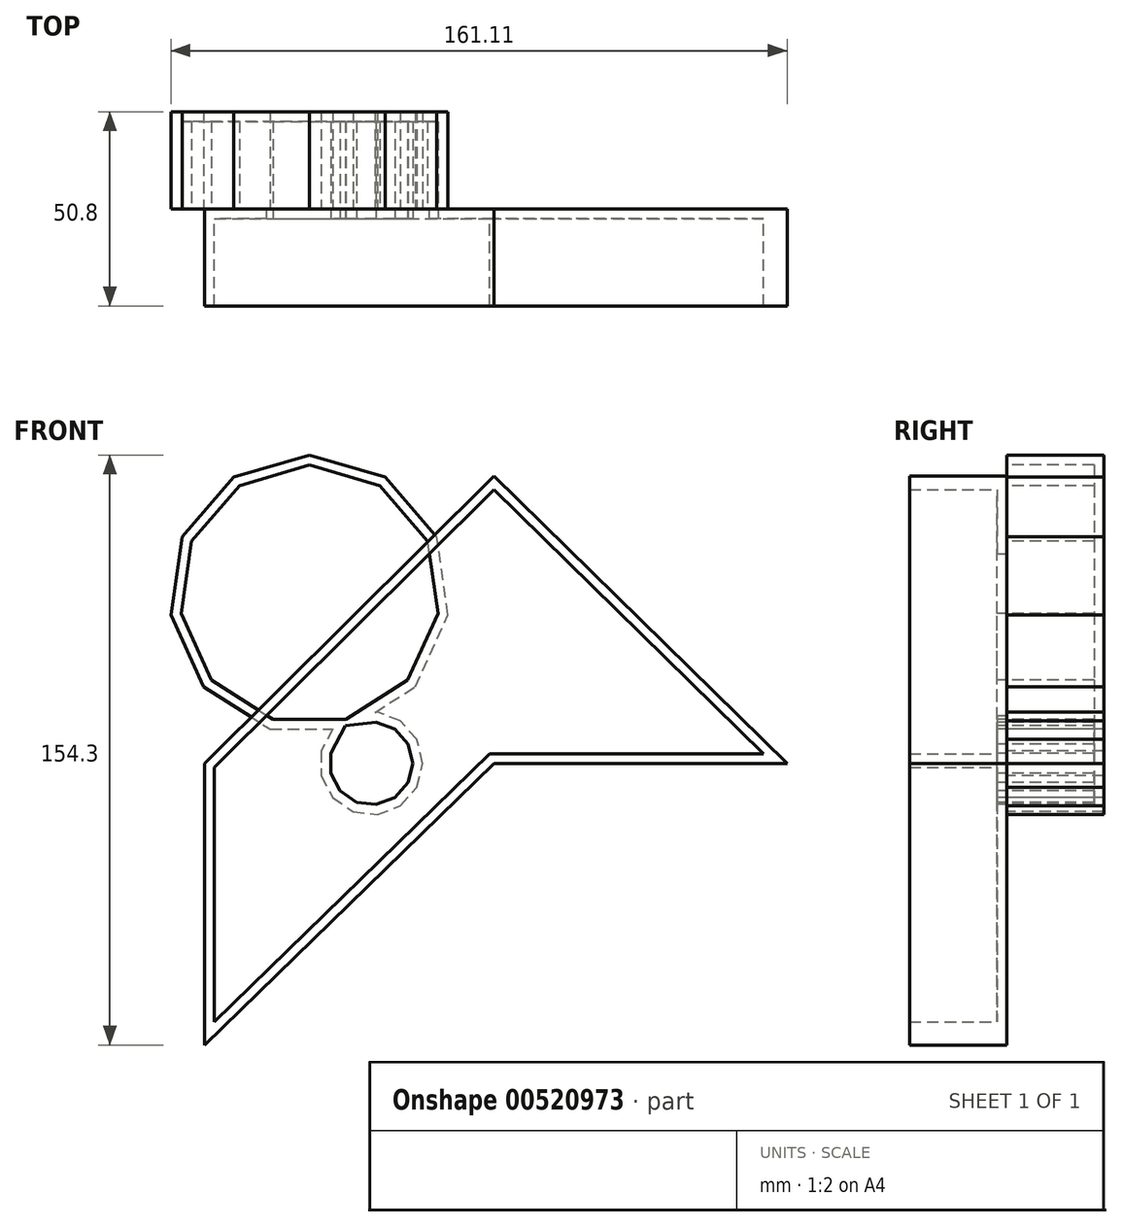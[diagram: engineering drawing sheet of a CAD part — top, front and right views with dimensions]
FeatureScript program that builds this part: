
annotation { "Feature Type Name" : "Feature", "Feature Type Description" : "" }
export const myFeature = defineFeature(function(context is Context, id is Id, definition is map)
    precondition{}
    {
        {
            var Q0;
            Q0=qCreatedBy(makeId("Front.planeOp"),FACE);
            var sketch = newSketch(context, id + "F0", { "sketchPlane" : qUnion([Q0])});
            skLineSegment(sketch, "E0", {"start": v(0, 75.14) * mm, "end": v(-75.6, 0) * mm});
            skLineSegment(sketch, "E1", {"start": v(-75.6, 0) * mm, "end": v(-75.6, -73.66) * mm});
            skLineSegment(sketch, "E2", {"start": v(-75.6, -73.66) * mm, "end": v(0, 0) * mm});
            skLineSegment(sketch, "E3", {"start": v(0, 0) * mm, "end": v(76.7, 0) * mm});
            skLineSegment(sketch, "E4", {"start": v(76.7, 0) * mm, "end": v(0, 75.14) * mm});
            skSolve(sketch);
        }
        {
            var Q0;
            Q0=makeQuery(id+"F0.imprint","IMPRINT",FACE,{"disambiguationData":[TD([[makeQuery(id+"F0.imprint","IMPRINT",EDGE,{"derivedFrom":sQuery(id+"F0.wireOp",EDGE,"E0")}),1.0]])]});
            extrude(context, id + "F1", {"entities" : qUnion([Q0]), "depth" : 25.4 * mm, "offsetDistance" : 25.4 * mm});
        }
        {
            var Q0;
            Q0=makeQuery(id+"F1.opExtrude","CAP_FACE",FACE,{"disambiguationData":[OSD([sQuery(id+"F0.wireOp",EDGE,"E0"),sQuery(id+"F0.wireOp",EDGE,"E1"),sQuery(id+"F0.wireOp",EDGE,"E2"),sQuery(id+"F0.wireOp",EDGE,"E3"),sQuery(id+"F0.wireOp",EDGE,"E4")])],"isStart":false});
            shell(context, id + "F2", {"entities" : qUnion([Q0]), "thickness" : 2.54 * mm});
        }
        {
            var Q0;
            Q0=makeQuery(id+"F1.opExtrude","CAP_FACE",FACE,{"disambiguationData":[OSD([sQuery(id+"F0.wireOp",EDGE,"E0"),sQuery(id+"F0.wireOp",EDGE,"E1"),sQuery(id+"F0.wireOp",EDGE,"E2"),sQuery(id+"F0.wireOp",EDGE,"E3"),sQuery(id+"F0.wireOp",EDGE,"E4")])],"isStart":true});
            var sketch = newSketch(context, id + "F3", { "sketchPlane" : qUnion([Q0])});
            skCircle(sketch, "E5.cCircle", {"center": v(32.06, 0) * mm, "radius": 13.08 * mm, "construction": true});
            skLineSegment(sketch, "E5.0", {"start": v(45.14, 3.22) * mm, "end": v(45.14, -3.22) * mm});
            skLineSegment(sketch, "E5.1", {"start": v(45.14, -3.22) * mm, "end": v(42.15, -8.93) * mm});
            skLineSegment(sketch, "E5.2", {"start": v(42.15, -8.93) * mm, "end": v(36.84, -12.6) * mm});
            skLineSegment(sketch, "E5.3", {"start": v(36.84, -12.6) * mm, "end": v(30.44, -13.37) * mm});
            skLineSegment(sketch, "E5.4", {"start": v(30.44, -13.37) * mm, "end": v(24.41, -11.09) * mm});
            skLineSegment(sketch, "E5.5", {"start": v(24.41, -11.09) * mm, "end": v(20.14, -6.26) * mm});
            skLineSegment(sketch, "E5.6", {"start": v(20.14, -6.26) * mm, "end": v(18.6, 0) * mm});
            skLineSegment(sketch, "E5.7", {"start": v(18.6, 0) * mm, "end": v(20.14, 6.26) * mm});
            skLineSegment(sketch, "E5.8", {"start": v(20.14, 6.26) * mm, "end": v(24.41, 11.09) * mm});
            skLineSegment(sketch, "E5.9", {"start": v(24.41, 11.09) * mm, "end": v(30.44, 13.37) * mm});
            skLineSegment(sketch, "E5.10", {"start": v(30.44, 13.37) * mm, "end": v(36.84, 12.6) * mm});
            skLineSegment(sketch, "E5.11", {"start": v(36.84, 12.6) * mm, "end": v(42.15, 8.93) * mm});
            skLineSegment(sketch, "E5.12", {"start": v(42.15, 8.93) * mm, "end": v(45.14, 3.22) * mm});
            skPoint(sketch, "E5.0.midPoint", {"position": v(45.14, 0) * mm});
            skCircle(sketch, "E6.cCircle", {"center": v(48.19, 44.05) * mm, "radius": 35.11 * mm, "construction": true});
            skLineSegment(sketch, "E6.0", {"start": v(58.5, 8.93) * mm, "end": v(37.88, 8.93) * mm});
            skLineSegment(sketch, "E6.1", {"start": v(37.88, 8.93) * mm, "end": v(20.53, 20.08) * mm});
            skLineSegment(sketch, "E6.2", {"start": v(20.53, 20.08) * mm, "end": v(11.97, 38.84) * mm});
            skLineSegment(sketch, "E6.3", {"start": v(11.97, 38.84) * mm, "end": v(14.9, 59.25) * mm});
            skLineSegment(sketch, "E6.4", {"start": v(14.9, 59.25) * mm, "end": v(28.4, 74.83) * mm});
            skLineSegment(sketch, "E6.5", {"start": v(28.4, 74.83) * mm, "end": v(48.19, 80.64) * mm});
            skLineSegment(sketch, "E6.6", {"start": v(48.19, 80.64) * mm, "end": v(67.97, 74.83) * mm});
            skLineSegment(sketch, "E6.7", {"start": v(67.97, 74.83) * mm, "end": v(81.48, 59.25) * mm});
            skLineSegment(sketch, "E6.8", {"start": v(81.48, 59.25) * mm, "end": v(84.41, 38.84) * mm});
            skLineSegment(sketch, "E6.9", {"start": v(84.41, 38.84) * mm, "end": v(75.85, 20.08) * mm});
            skLineSegment(sketch, "E6.10", {"start": v(75.85, 20.08) * mm, "end": v(58.5, 8.93) * mm});
            skPoint(sketch, "E6.0.midPoint", {"position": v(48.19, 8.93) * mm});
            skSolve(sketch);
        }
        {
            var Q0;
            Q0 = qSketchRegion(id + "F3", true);
            extrude(context, id + "F4", {"entities" : qUnion([Q0]), "operationType" : NewBodyOperationType.ADD, "depth" : 25.4 * mm, "offsetDistance" : 25.4 * mm});
        }
        {
            var Q0;
            Q0=makeQuery(id+"F4.opExtrude","CAP_FACE",FACE,{"disambiguationData":[OSD([sQuery(id+"F3.wireOp",EDGE,"E5.0"),sQuery(id+"F3.wireOp",EDGE,"E5.1"),sQuery(id+"F3.wireOp",EDGE,"E5.2"),sQuery(id+"F3.wireOp",EDGE,"E5.3"),sQuery(id+"F3.wireOp",EDGE,"E5.4"),sQuery(id+"F3.wireOp",EDGE,"E5.5"),sQuery(id+"F3.wireOp",EDGE,"E5.6"),sQuery(id+"F3.wireOp",EDGE,"E5.7"),sQuery(id+"F3.wireOp",EDGE,"E5.8"),sQuery(id+"F3.wireOp",EDGE,"E5.9"),sQuery(id+"F3.wireOp",EDGE,"E5.10"),sQuery(id+"F3.wireOp",EDGE,"E5.12"),sQuery(id+"F3.wireOp",EDGE,"E6.0"),sQuery(id+"F3.wireOp",EDGE,"E6.1"),sQuery(id+"F3.wireOp",EDGE,"E6.2"),sQuery(id+"F3.wireOp",EDGE,"E6.3"),sQuery(id+"F3.wireOp",EDGE,"E6.4"),sQuery(id+"F3.wireOp",EDGE,"E6.5"),sQuery(id+"F3.wireOp",EDGE,"E6.6"),sQuery(id+"F3.wireOp",EDGE,"E6.7"),sQuery(id+"F3.wireOp",EDGE,"E6.8"),sQuery(id+"F3.wireOp",EDGE,"E6.9"),sQuery(id+"F3.wireOp",EDGE,"E6.10")])],"isStart":true});
            var Q1;
            Q1=makeQuery(id+"F2.opShell","OFFSET_FACE",FACE,{"disambiguationData":[OSD([sQuery(id+"F0.wireOp",EDGE,"E0"),sQuery(id+"F0.wireOp",EDGE,"E1"),sQuery(id+"F0.wireOp",EDGE,"E2"),sQuery(id+"F0.wireOp",EDGE,"E3"),sQuery(id+"F0.wireOp",EDGE,"E4")])]});
            shell(context, id + "F5", {"entities" : qUnion([Q0, Q1]), "thickness" : 2.54 * mm});
        }
    });
